# Revit family: РГК-100
name_source: partatom
category: Арматура трубопроводов
units: mm (PartAtom-declared; Revit-internal decimal feet)

## family parameters
Всегда вертикально = Да
На основе рабочей плоскости = Нет
Общий = Нет
При загрузке вырезать с полостями = Нет
Размер круглого соединителя = Использовать диаметр
Тип детали = Клапан - Вставляется

## types (6) — shared parameters
ADSK_Единица измерения = шт.
ADSK_Завод-изготовитель = РУП "БЕЛГАЗТЕХНИКА"
ADSK_Количество = 1
ADSK_Масса_Текст = 90,0 кг
zero-valued in all types: Отметка по умолчанию

## per-type parameters (varying)
| type | ADSK_Диапазон выходного давления, МПа | ADSK_Марка | ADSK_Наименование | исполнение 00, 02, 04 | исполнение 01, 03, 05 |
| исполнение 04 | 0,3-0,6 | РГК-100-04 | Регулятор РГК-100-04 ТУ BY 100270876.130-2006 | Да | Нет |
| исполнение 00 | 0,01-0,05 | РГК-100-00 | Регулятор РГК-100-00 ТУ BY 100270876.130-2006 | Да | Нет |
| исполнение 01 | 0,01-0,05 | РГК-100-01 | Регулятор РГК-100-01 ТУ BY 100270876.130-2006 | Нет | Да |
| исполнение 02 | 0,05-0,3 | РГК-100-02 | Регулятор РГК-100-02 ТУ BY 100270876.130-2006 | Да | Нет |
| исполнение 03 | 0,05-0,3 | РГК-100-03 | Регулятор РГК-100-03 ТУ BY 100270876.130-2006 | Нет | Да |
| исполнение 05 | 0,3-0,6 | РГК-100-05 | Регулятор РГК-100-05 ТУ BY 100270876.130-2006 | Нет | Да |
